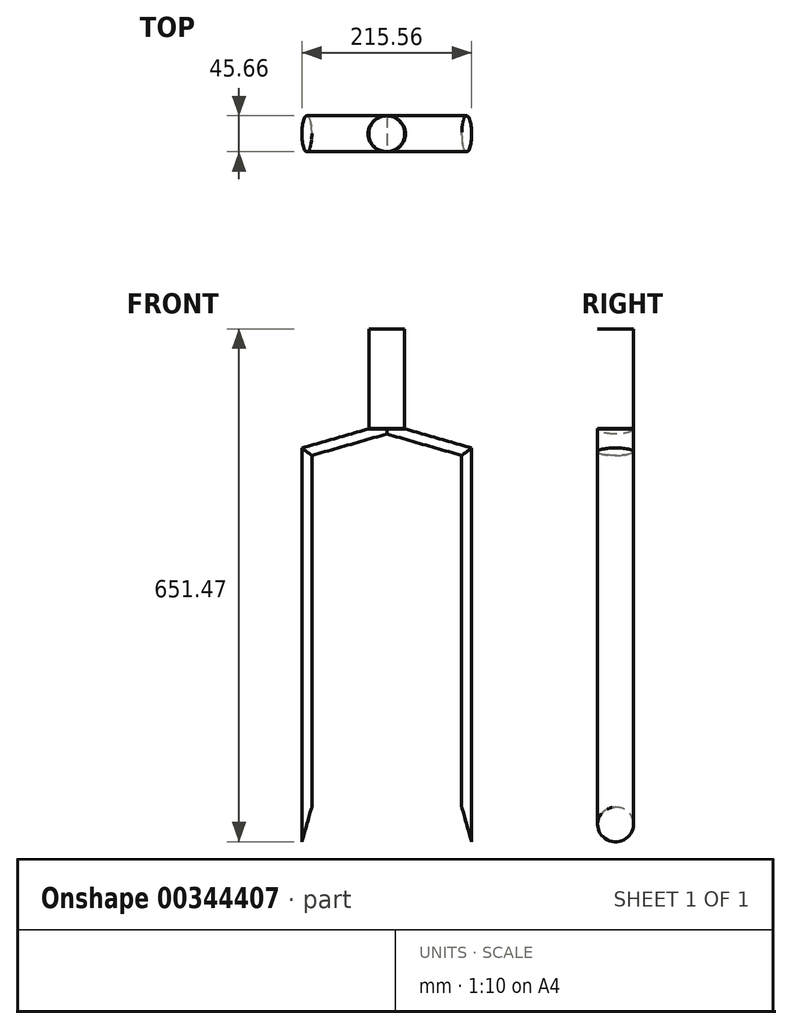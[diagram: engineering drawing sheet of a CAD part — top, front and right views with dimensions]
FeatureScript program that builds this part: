
annotation { "Feature Type Name" : "Feature", "Feature Type Description" : "" }
export const myFeature = defineFeature(function(context is Context, id is Id, definition is map)
    precondition{}
    {
        {
            var Q0;
            Q0=qCreatedBy(makeId("Top.planeOp"),FACE);
            var sketch = newSketch(context, id + "F0", { "sketchPlane" : qUnion([Q0])});
            skCircle(sketch, "E0", {"center": v(0, 0) * mm, "radius": 22.83 * mm});
            skSolve(sketch);
        }
        {
            var Q0;
            Q0=makeQuery(id+"F0.imprint","IMPRINT",FACE,{"disambiguationData":[TD([[makeQuery(id+"F0.imprint","IMPRINT",EDGE,{"derivedFrom":sQuery(id+"F0.wireOp",EDGE,"E0")}),1.0]])]});
            var Q1;
            Q1=sQuery(id+"F0.wireOp",EDGE,"E0");
            extrude(context, id + "F1", {"entities" : qUnion([Q0]), "surfaceEntities" : qUnion([Q1]), "endBound" : BoundingType.SYMMETRIC, "depth" : 127 * mm});
        }
        {
            var Q0;
            Q0=qCreatedBy(makeId("Front.planeOp"),FACE);
            var sketch = newSketch(context, id + "F2", { "sketchPlane" : qUnion([Q0])});
            skLineSegment(sketch, "E1", {"start": v(0, -63.21) * mm, "end": v(-101.77, -92.37) * mm});
            skFitSpline(sketch, "E2", {"points": [v(-101.77, -92.37) * mm, v(-101.77, -566.99) * mm], "startDerivative": vector(0, -157.22) * mm, "endDerivative": vector(0, -157.22) * mm});
            skLineSegment(sketch, "E3.MirrorCS", {"start": v(0, -63.21) * mm, "end": v(101.77, -92.37) * mm});
            skFitSpline(sketch, "E4.MirrorCS", {"points": [v(101.77, -92.37) * mm, v(101.77, -566.99) * mm], "startDerivative": vector(0, -157.22) * mm, "endDerivative": vector(0, -157.22) * mm});
            skSolve(sketch);
        }
        {
            var Q0;
            Q0=makeQuery(id+"F1.opExtrude","SWEPT_BODY",BODY,{"disambiguationData":[OSD([sQuery(id+"F0.wireOp",EDGE,"E0")])]});
            var Q1;
            Q1=qCreatedBy(makeId("Right.planeOp"),FACE);
            mirror(context, id + "F3", {"operationType" : NewBodyOperationType.ADD, "entities" : qUnion([Q0]), "mirrorPlane" : qUnion([Q1])});
        }
        {
            var Q0;
            Q0=makeQuery(id+"F1.opExtrude","CAP_FACE",FACE,{"disambiguationData":[OSD([sQuery(id+"F0.wireOp",EDGE,"E0")])],"isStart":true});
            var Q1;
            Q1=sQuery(id+"F2.wireOp",EDGE,"E1");
            var Q2;
            Q2=sQuery(id+"F2.wireOp",EDGE,"E2");
            sweep(context, id + "F4", {"operationType" : NewBodyOperationType.ADD, "profiles" : qUnion([Q0]), "path" : qUnion([Q1, Q2])});
        }
        {
            var Q0;
            Q0=makeQuery(id+"F1.opExtrude","SWEPT_BODY",BODY,{"disambiguationData":[OSD([sQuery(id+"F0.wireOp",EDGE,"E0")])]});
            var Q1;
            Q1=qCreatedBy(makeId("Right.planeOp"),FACE);
            mirror(context, id + "F5", {"operationType" : NewBodyOperationType.ADD, "entities" : qUnion([Q0]), "mirrorPlane" : qUnion([Q1])});
        }
    });
